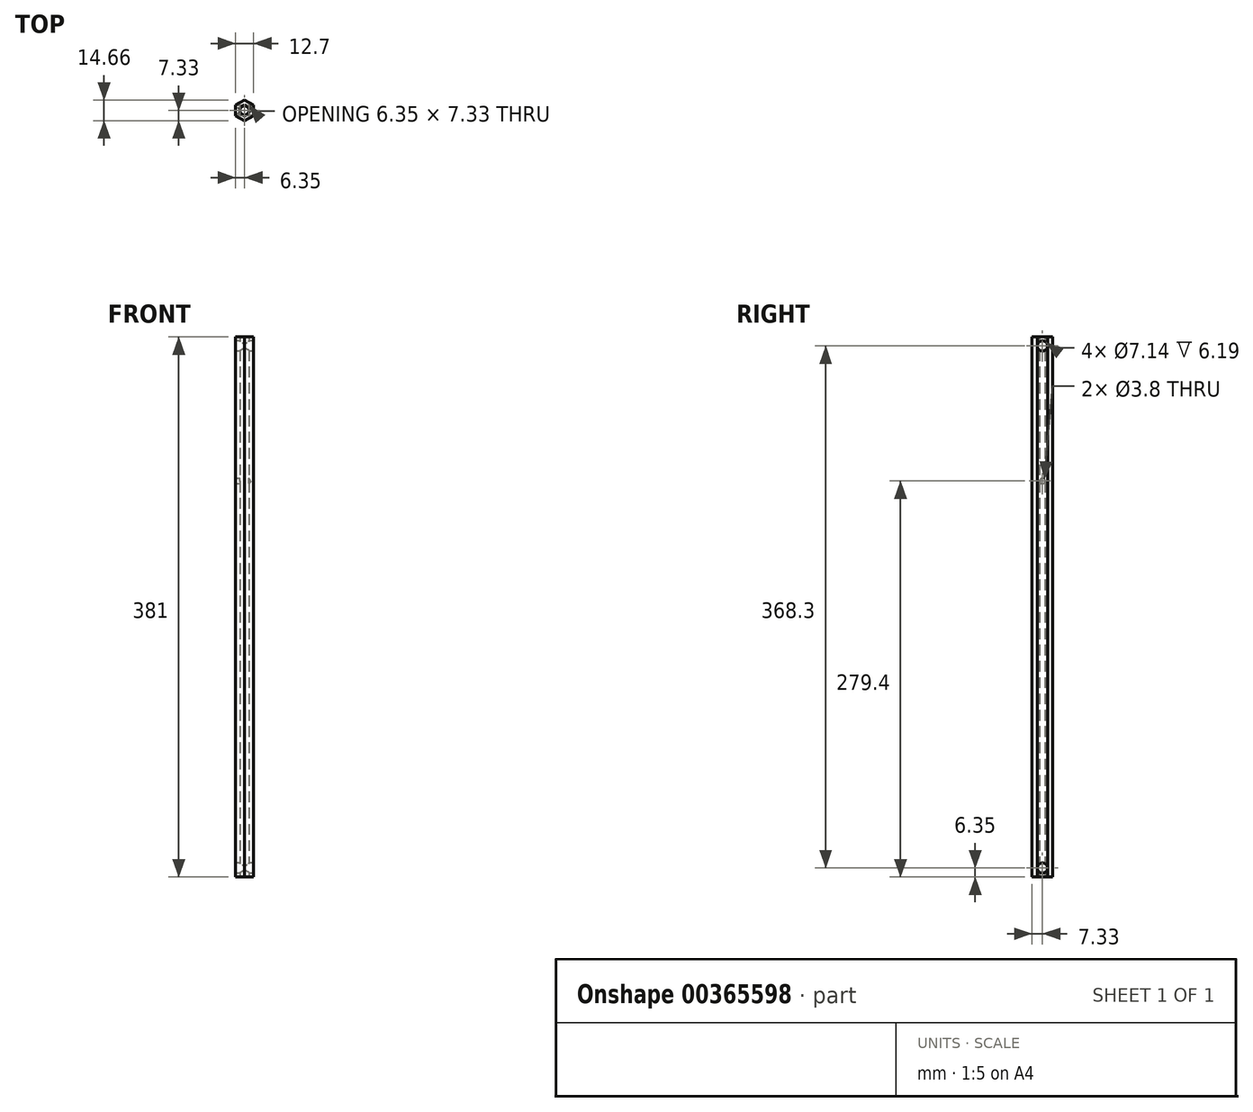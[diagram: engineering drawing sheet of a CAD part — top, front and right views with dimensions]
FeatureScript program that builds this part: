
annotation { "Feature Type Name" : "Feature", "Feature Type Description" : "" }
export const myFeature = defineFeature(function(context is Context, id is Id, definition is map)
    precondition{}
    {
        {
            var Q0;
            Q0=qCreatedBy(makeId("Top.planeOp"),FACE);
            var sketch = newSketch(context, id + "F0", { "sketchPlane" : qUnion([Q0])});
            skCircle(sketch, "E0.cCircle", {"center": v(0, 0) * mm, "radius": 3.18 * mm, "construction": true});
            skLineSegment(sketch, "E0.0", {"start": v(3.18, 1.83) * mm, "end": v(3.18, -1.83) * mm});
            skLineSegment(sketch, "E0.1", {"start": v(3.18, -1.83) * mm, "end": v(0, -3.67) * mm});
            skLineSegment(sketch, "E0.2", {"start": v(0, -3.67) * mm, "end": v(-3.18, -1.83) * mm});
            skLineSegment(sketch, "E0.3", {"start": v(-3.18, -1.83) * mm, "end": v(-3.18, 1.83) * mm});
            skLineSegment(sketch, "E0.4", {"start": v(-3.18, 1.83) * mm, "end": v(0, 3.67) * mm});
            skLineSegment(sketch, "E0.5", {"start": v(0, 3.67) * mm, "end": v(3.18, 1.83) * mm});
            skPoint(sketch, "E0.0.midPoint", {"position": v(3.18, 0) * mm});
            skCircle(sketch, "E1.cCircle", {"center": v(0, 0) * mm, "radius": 6.35 * mm, "construction": true});
            skLineSegment(sketch, "E1.0", {"start": v(0, 7.33) * mm, "end": v(6.35, 3.67) * mm});
            skLineSegment(sketch, "E1.1", {"start": v(6.35, 3.67) * mm, "end": v(6.35, -3.67) * mm});
            skLineSegment(sketch, "E1.2", {"start": v(6.35, -3.67) * mm, "end": v(0, -7.33) * mm});
            skLineSegment(sketch, "E1.3", {"start": v(0, -7.33) * mm, "end": v(-6.35, -3.67) * mm});
            skLineSegment(sketch, "E1.4", {"start": v(-6.35, -3.67) * mm, "end": v(-6.35, 3.67) * mm});
            skLineSegment(sketch, "E1.5", {"start": v(-6.35, 3.67) * mm, "end": v(0, 7.33) * mm});
            skPoint(sketch, "E1.0.midPoint", {"position": v(3.17, 5.5) * mm});
            skSolve(sketch);
        }
        {
            var Q0;
            Q0=makeQuery(id+"F0.imprint","IMPRINT",FACE,{"disambiguationData":[TD([[makeQuery(id+"F0.imprint","IMPRINT",EDGE,{"derivedFrom":sQuery(id+"F0.wireOp",EDGE,"E0.0")}),1.0]])]});
            extrude(context, id + "F1", {"entities" : qUnion([Q0]), "depth" : 381 * mm, "offsetDistance" : 25.4 * mm});
        }
        {
            var Q0;
            Q0=makeQuery(id+"F1.opExtrude","SWEPT_FACE",FACE,{"disambiguationData":[OSD([sQuery(id+"F0.wireOp",EDGE,"E1.1")])]});
            var sketch = newSketch(context, id + "F2", { "sketchPlane" : qUnion([Q0])});
            skPoint(sketch, "E2", {"position": v(0, 6.35) * mm});
            skPoint(sketch, "E3", {"position": v(0, 374.65) * mm});
            skSolve(sketch);
        }
        {
            var Q0;
            Q0=sQuery(id+"F2.wireOp",VERTEX,"E3");
            var Q1;
            Q1=sQuery(id+"F2.wireOp",VERTEX,"E2");
            var Q2;
            Q2=makeQuery(id+"F1.opExtrude","SWEPT_BODY",BODY,{"disambiguationData":[OSD([sQuery(id+"F0.wireOp",EDGE,"E0.0"),sQuery(id+"F0.wireOp",EDGE,"E0.1"),sQuery(id+"F0.wireOp",EDGE,"E0.2"),sQuery(id+"F0.wireOp",EDGE,"E0.3"),sQuery(id+"F0.wireOp",EDGE,"E0.4"),sQuery(id+"F0.wireOp",EDGE,"E0.5"),sQuery(id+"F0.wireOp",EDGE,"E1.0"),sQuery(id+"F0.wireOp",EDGE,"E1.1"),sQuery(id+"F0.wireOp",EDGE,"E1.2"),sQuery(id+"F0.wireOp",EDGE,"E1.3"),sQuery(id+"F0.wireOp",EDGE,"E1.4"),sQuery(id+"F0.wireOp",EDGE,"E1.5")])]});
            hole(context, id + "F3", {"style" : HoleStyle.SIMPLE, "endStyle" : HoleEndStyle.THROUGH, "standardTappedOrClearance" : lookupTablePath({ "fit" : "Normal (ASME)", "standard" : "ANSI", "size" : "1/4", "type" : "Clearance" }), "standardBlindInLast" : lookupTablePath({ "fit" : "Normal", "standard" : "ANSI", "engagement" : "75%", "pitch" : "20 tpi", "size" : "1/4", "type" : "Clearance & tapped" }), "holeDiameter" : 7.14 * mm, "majorDiameter" : 6.35 * mm, "isTappedThrough" : true, "tappedDepth" : 12.7 * mm, "tapClearance" : 3, "locations" : qUnion([Q0, Q1]), "scope" : qUnion([Q2]), "startStyle" : HoleStartStyle.SKETCH});
        }
        {
            var Q0;
            Q0=makeQuery(id+"F1.opExtrude","SWEPT_FACE",FACE,{"disambiguationData":[OSD([sQuery(id+"F0.wireOp",EDGE,"E1.4")])]});
            var sketch = newSketch(context, id + "F4", { "sketchPlane" : qUnion([Q0])});
            skPoint(sketch, "E4", {"position": v(0, 279.4) * mm});
            skSolve(sketch);
        }
        {
            var Q0;
            Q0=sQuery(id+"F4.wireOp",VERTEX,"E4");
            var Q1;
            Q1=makeQuery(id+"F1.opExtrude","SWEPT_BODY",BODY,{"disambiguationData":[OSD([sQuery(id+"F0.wireOp",EDGE,"E0.0"),sQuery(id+"F0.wireOp",EDGE,"E0.1"),sQuery(id+"F0.wireOp",EDGE,"E0.2"),sQuery(id+"F0.wireOp",EDGE,"E0.3"),sQuery(id+"F0.wireOp",EDGE,"E0.4"),sQuery(id+"F0.wireOp",EDGE,"E0.5"),sQuery(id+"F0.wireOp",EDGE,"E1.0"),sQuery(id+"F0.wireOp",EDGE,"E1.1"),sQuery(id+"F0.wireOp",EDGE,"E1.2"),sQuery(id+"F0.wireOp",EDGE,"E1.3"),sQuery(id+"F0.wireOp",EDGE,"E1.4"),sQuery(id+"F0.wireOp",EDGE,"E1.5")])]});
            hole(context, id + "F5", {"style" : HoleStyle.SIMPLE, "endStyle" : HoleEndStyle.BLIND, "standardTappedOrClearance" : lookupTablePath({ "standard" : "ANSI", "engagement" : "75%", "pitch" : "24 tpi", "size" : "#10", "type" : "Tapped" }), "standardBlindInLast" : lookupTablePath({ "standard" : "ANSI", "fit" : "Normal", "engagement" : "75%", "pitch" : "24 tpi", "size" : "#10", "type" : "Clearance & tapped" }), "holeDiameter" : 3.8 * mm, "majorDiameter" : 4.83 * mm, "showTappedDepth" : true, "holeDepth" : 9.54 * mm, "isTappedThrough" : true, "tappedDepth" : 6.36 * mm, "tapClearance" : 3, "locations" : qUnion([Q0]), "scope" : qUnion([Q1]), "startStyle" : HoleStartStyle.SKETCH});
        }
    });
